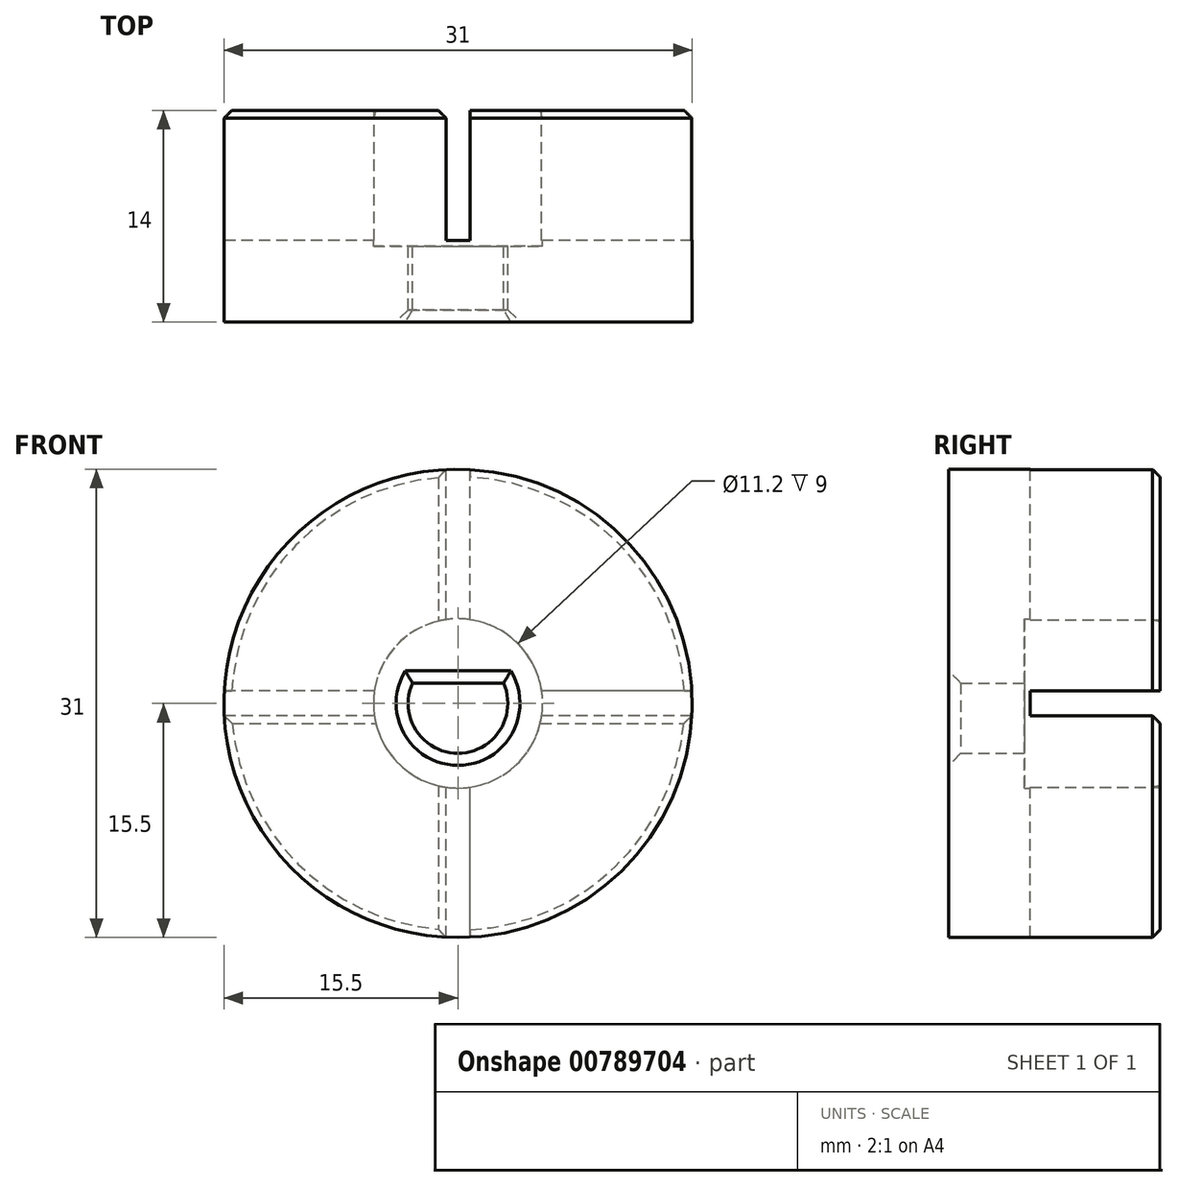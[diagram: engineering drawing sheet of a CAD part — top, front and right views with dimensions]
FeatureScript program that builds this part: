
annotation { "Feature Type Name" : "Feature", "Feature Type Description" : "" }
export const myFeature = defineFeature(function(context is Context, id is Id, definition is map)
    precondition{}
    {
        {
            var Q0;
            Q0=qCreatedBy(makeId("Front.planeOp"),FACE);
            var sketch = newSketch(context, id + "F0", { "sketchPlane" : qUnion([Q0])});
            skCircle(sketch, "E0", {"center": v(0, 0) * mm, "radius": 15.5 * mm});
            skArc(sketch, "E1", {"start": v(-3.01, 1.35) * mm, "mid": v(0, -3.3) * mm, "end": v(3.01, 1.35) * mm});
            skLineSegment(sketch, "E2", {"start": v(-3.01, 1.35) * mm, "end": v(3.01, 1.35) * mm});
            skSolve(sketch);
        }
        {
            var Q0;
            Q0=makeQuery(id+"F0.imprint","IMPRINT",FACE,{"disambiguationData":[TD([[makeQuery(id+"F0.imprint","IMPRINT",EDGE,{"derivedFrom":sQuery(id+"F0.wireOp",EDGE,"E0")}),1.0]])]});
            extrude(context, id + "F1", {"entities" : qUnion([Q0]), "depth" : 14 * mm, "offsetDistance" : 25 * mm});
        }
        {
            var Q0;
            Q0=qCreatedBy(makeId("Front.planeOp"),FACE);
            var sketch = newSketch(context, id + "F2", { "sketchPlane" : qUnion([Q0])});
            skLineSegment(sketch, "E3.bottom", {"start": v(18, -0.82) * mm, "end": v(-18, -0.83) * mm});
            skLineSegment(sketch, "E3.top", {"start": v(18, 0.83) * mm, "end": v(-18, 0.82) * mm});
            skLineSegment(sketch, "E3.left", {"start": v(18, -0.82) * mm, "end": v(18, 0.83) * mm});
            skLineSegment(sketch, "E3.right", {"start": v(-18, -0.83) * mm, "end": v(-18, 0.82) * mm});
            skSolve(sketch);
        }
        {
            var Q0;
            Q0=makeQuery(id+"F2.imprint","IMPRINT",FACE,{"disambiguationData":[TD([[makeQuery(id+"F2.imprint","IMPRINT",EDGE,{"derivedFrom":sQuery(id+"F2.wireOp",EDGE,"E3.bottom")}),-1.0]])]});
            extrude(context, id + "F3", {"entities" : qUnion([Q0]), "operationType" : NewBodyOperationType.REMOVE, "depth" : 8.6 * mm, "offsetDistance" : 25 * mm});
        }
        {
            var Q0;
            Q0=qCreatedBy(makeId("Front.planeOp"),FACE);
            var sketch = newSketch(context, id + "F4", { "sketchPlane" : qUnion([Q0])});
            skLineSegment(sketch, "E4.bottom", {"start": v(0.8, -20) * mm, "end": v(-0.8, -20) * mm});
            skLineSegment(sketch, "E4.top", {"start": v(0.8, 20) * mm, "end": v(-0.8, 20) * mm});
            skLineSegment(sketch, "E4.left", {"start": v(0.8, -20) * mm, "end": v(0.8, 20) * mm});
            skLineSegment(sketch, "E4.right", {"start": v(-0.8, -20) * mm, "end": v(-0.8, 20) * mm});
            skSolve(sketch);
        }
        {
            var Q0;
            Q0 = qSketchRegion(id + "F4", true);
            extrude(context, id + "F5", {"entities" : qUnion([Q0]), "operationType" : NewBodyOperationType.REMOVE, "depth" : 8.6 * mm, "offsetDistance" : 25 * mm});
        }
        {
            var Q0;
            Q0=qCreatedBy(makeId("Front.planeOp"),FACE);
            var sketch = newSketch(context, id + "F6", { "sketchPlane" : qUnion([Q0])});
            skCircle(sketch, "E5", {"center": v(0, 0) * mm, "radius": 5.6 * mm});
            skSolve(sketch);
        }
        {
            var Q0;
            Q0=makeQuery(id+"F6.imprint","IMPRINT",FACE,{"disambiguationData":[TD([[makeQuery(id+"F6.imprint","IMPRINT",EDGE,{"derivedFrom":sQuery(id+"F6.wireOp",EDGE,"E5")}),1.0]])]});
            extrude(context, id + "F7", {"entities" : qUnion([Q0]), "operationType" : NewBodyOperationType.REMOVE, "depth" : 9 * mm, "offsetDistance" : 25 * mm});
        }
        {
            var Q0;
            Q0=makeQuery(id+"F1.opExtrude","CAP_EDGE",EDGE,{"disambiguationData":[OSD([sQuery(id+"F0.wireOp",EDGE,"E2")])],"isStart":false});
            var Q1;
            Q1=makeQuery(id+"F1.opExtrude","CAP_EDGE",EDGE,{"disambiguationData":[OSD([sQuery(id+"F0.wireOp",EDGE,"E1")])],"isStart":false});
            chamfer(context, id + "F8", {"entities" : qUnion([Q0, Q1]), "width" : 0.8 * mm, "tangentPropagation" : true});
        }
        {
            var Q0;
            Q0=makeQuery(id+"F3.boolean.opBoolean","COPY",EDGE,{"disambiguationData":[OD(0.0)],"derivedFrom":makeQuery(id+"F3.opExtrude","CAP_EDGE",EDGE,{"disambiguationData":[OSD([sQuery(id+"F2.wireOp",EDGE,"E3.top")])],"isStart":true})});
            var Q1;
            Q1=makeQuery(id+"F3.boolean.opBoolean","COPY",EDGE,{"disambiguationData":[OD(0.0)],"derivedFrom":makeQuery(id+"F3.opExtrude","CAP_EDGE",EDGE,{"disambiguationData":[OSD([sQuery(id+"F2.wireOp",EDGE,"E3.bottom")])],"isStart":true})});
            var Q2;
            {var subQ1=sQuery(id+"F0.wireOp",EDGE,"E1");var subQ2=sQuery(id+"F4.wireOp",EDGE,"E4.right");Q2=makeQuery(id+"F5.boolean.opBoolean","COPY",EDGE,{"disambiguationData":[TD([makeQuery(id+"F1.opExtrude","SWEPT_FACE",FACE,{"disambiguationData":[OSD([subQ1])]})])],"derivedFrom":makeQuery(id+"F5.opExtrude","CAP_EDGE",EDGE,{"disambiguationData":[OSD([subQ2])],"isStart":true})});}
            var Q3;
            {var subQ1=sQuery(id+"F0.wireOp",EDGE,"E1");var subQ2=sQuery(id+"F4.wireOp",EDGE,"E4.left");Q3=makeQuery(id+"F5.boolean.opBoolean","COPY",EDGE,{"disambiguationData":[TD([makeQuery(id+"F1.opExtrude","SWEPT_FACE",FACE,{"disambiguationData":[OSD([subQ1])]})])],"derivedFrom":makeQuery(id+"F5.opExtrude","CAP_EDGE",EDGE,{"disambiguationData":[OSD([subQ2])],"isStart":true})});}
            var Q4;
            {var subQ3=sQuery(id+"F6.wireOp",EDGE,"E5");Q4=makeQuery(id+"F7.boolean.opBoolean","COPY",EDGE,{"disambiguationData":[TD([makeQuery(id+"F3.boolean.opBoolean","COPY",FACE,{"disambiguationData":[OD(1.0)],"derivedFrom":makeQuery(id+"F3.opExtrude","SWEPT_FACE",FACE,{"disambiguationData":[OSD([sQuery(id+"F2.wireOp",EDGE,"E3.bottom")])]})})])],"derivedFrom":makeQuery(id+"F7.opExtrude","CAP_EDGE",EDGE,{"disambiguationData":[OSD([subQ3])],"isStart":true})});}
            var Q5;
            Q5=makeQuery(id+"F3.boolean.opBoolean","COPY",EDGE,{"disambiguationData":[OD(1.0)],"derivedFrom":makeQuery(id+"F3.opExtrude","CAP_EDGE",EDGE,{"disambiguationData":[OSD([sQuery(id+"F2.wireOp",EDGE,"E3.bottom")])],"isStart":true})});
            var Q6;
            {var subQ0=sQuery(id+"F0.wireOp",EDGE,"E0");var subQ3=makeQuery(id+"F3.opExtrude","SWEPT_FACE",FACE,{"disambiguationData":[OSD([sQuery(id+"F2.wireOp",EDGE,"E3.bottom")])]});Q6=makeQuery(id+"F5.boolean.opBoolean","SPLIT",EDGE,{"disambiguationData":[TD([makeQuery(id+"F3.boolean.opBoolean","COPY",FACE,{"disambiguationData":[OD(1.0)],"derivedFrom":subQ3})])],"derivedFrom":makeQuery(id+"F3.boolean.opBoolean","SPLIT",EDGE,{"disambiguationData":[TD([subQ3])],"derivedFrom":makeQuery(id+"F1.opExtrude","CAP_EDGE",EDGE,{"disambiguationData":[OSD([subQ0])],"isStart":true})})});}
            var Q7;
            {var subQ0=sQuery(id+"F0.wireOp",EDGE,"E0");var subQ3=makeQuery(id+"F3.opExtrude","SWEPT_FACE",FACE,{"disambiguationData":[OSD([sQuery(id+"F2.wireOp",EDGE,"E3.bottom")])]});Q7=makeQuery(id+"F5.boolean.opBoolean","SPLIT",EDGE,{"disambiguationData":[TD([makeQuery(id+"F3.boolean.opBoolean","COPY",FACE,{"disambiguationData":[OD(0.0)],"derivedFrom":subQ3})])],"derivedFrom":makeQuery(id+"F3.boolean.opBoolean","SPLIT",EDGE,{"disambiguationData":[TD([subQ3])],"derivedFrom":makeQuery(id+"F1.opExtrude","CAP_EDGE",EDGE,{"disambiguationData":[OSD([subQ0])],"isStart":true})})});}
            var Q8;
            {var subQ3=sQuery(id+"F6.wireOp",EDGE,"E5");Q8=makeQuery(id+"F7.boolean.opBoolean","COPY",EDGE,{"disambiguationData":[TD([makeQuery(id+"F3.boolean.opBoolean","COPY",FACE,{"disambiguationData":[OD(0.0)],"derivedFrom":makeQuery(id+"F3.opExtrude","SWEPT_FACE",FACE,{"disambiguationData":[OSD([sQuery(id+"F2.wireOp",EDGE,"E3.bottom")])]})})])],"derivedFrom":makeQuery(id+"F7.opExtrude","CAP_EDGE",EDGE,{"disambiguationData":[OSD([subQ3])],"isStart":true})});}
            var Q9;
            {var subQ3=sQuery(id+"F6.wireOp",EDGE,"E5");Q9=makeQuery(id+"F7.boolean.opBoolean","COPY",EDGE,{"disambiguationData":[TD([makeQuery(id+"F3.boolean.opBoolean","COPY",FACE,{"disambiguationData":[OD(0.0)],"derivedFrom":makeQuery(id+"F3.opExtrude","SWEPT_FACE",FACE,{"disambiguationData":[OSD([sQuery(id+"F2.wireOp",EDGE,"E3.top")])]})})])],"derivedFrom":makeQuery(id+"F7.opExtrude","CAP_EDGE",EDGE,{"disambiguationData":[OSD([subQ3])],"isStart":true})});}
            var Q10;
            {var subQ0=sQuery(id+"F0.wireOp",EDGE,"E0");var subQ3=makeQuery(id+"F3.opExtrude","SWEPT_FACE",FACE,{"disambiguationData":[OSD([sQuery(id+"F2.wireOp",EDGE,"E3.top")])]});Q10=makeQuery(id+"F5.boolean.opBoolean","SPLIT",EDGE,{"disambiguationData":[TD([makeQuery(id+"F3.boolean.opBoolean","COPY",FACE,{"disambiguationData":[OD(0.0)],"derivedFrom":subQ3})])],"derivedFrom":makeQuery(id+"F3.boolean.opBoolean","SPLIT",EDGE,{"disambiguationData":[TD([subQ3])],"derivedFrom":makeQuery(id+"F1.opExtrude","CAP_EDGE",EDGE,{"disambiguationData":[OSD([subQ0])],"isStart":true})})});}
            var Q11;
            {var subQ1=sQuery(id+"F0.wireOp",EDGE,"E2");var subQ2=sQuery(id+"F4.wireOp",EDGE,"E4.right");Q11=makeQuery(id+"F5.boolean.opBoolean","COPY",EDGE,{"disambiguationData":[TD([makeQuery(id+"F1.opExtrude","SWEPT_FACE",FACE,{"disambiguationData":[OSD([subQ1])]})])],"derivedFrom":makeQuery(id+"F5.opExtrude","CAP_EDGE",EDGE,{"disambiguationData":[OSD([subQ2])],"isStart":true})});}
            var Q12;
            {var subQ1=sQuery(id+"F0.wireOp",EDGE,"E2");var subQ2=sQuery(id+"F4.wireOp",EDGE,"E4.left");Q12=makeQuery(id+"F5.boolean.opBoolean","COPY",EDGE,{"disambiguationData":[TD([makeQuery(id+"F1.opExtrude","SWEPT_FACE",FACE,{"disambiguationData":[OSD([subQ1])]})])],"derivedFrom":makeQuery(id+"F5.opExtrude","CAP_EDGE",EDGE,{"disambiguationData":[OSD([subQ2])],"isStart":true})});}
            var Q13;
            {var subQ3=sQuery(id+"F6.wireOp",EDGE,"E5");Q13=makeQuery(id+"F7.boolean.opBoolean","COPY",EDGE,{"disambiguationData":[TD([makeQuery(id+"F3.boolean.opBoolean","COPY",FACE,{"disambiguationData":[OD(1.0)],"derivedFrom":makeQuery(id+"F3.opExtrude","SWEPT_FACE",FACE,{"disambiguationData":[OSD([sQuery(id+"F2.wireOp",EDGE,"E3.top")])]})})])],"derivedFrom":makeQuery(id+"F7.opExtrude","CAP_EDGE",EDGE,{"disambiguationData":[OSD([subQ3])],"isStart":true})});}
            var Q14;
            Q14=makeQuery(id+"F3.boolean.opBoolean","COPY",EDGE,{"disambiguationData":[OD(1.0)],"derivedFrom":makeQuery(id+"F3.opExtrude","CAP_EDGE",EDGE,{"disambiguationData":[OSD([sQuery(id+"F2.wireOp",EDGE,"E3.top")])],"isStart":true})});
            var Q15;
            {var subQ0=sQuery(id+"F0.wireOp",EDGE,"E0");var subQ3=makeQuery(id+"F3.opExtrude","SWEPT_FACE",FACE,{"disambiguationData":[OSD([sQuery(id+"F2.wireOp",EDGE,"E3.top")])]});Q15=makeQuery(id+"F5.boolean.opBoolean","SPLIT",EDGE,{"disambiguationData":[TD([makeQuery(id+"F3.boolean.opBoolean","COPY",FACE,{"disambiguationData":[OD(1.0)],"derivedFrom":subQ3})])],"derivedFrom":makeQuery(id+"F3.boolean.opBoolean","SPLIT",EDGE,{"disambiguationData":[TD([subQ3])],"derivedFrom":makeQuery(id+"F1.opExtrude","CAP_EDGE",EDGE,{"disambiguationData":[OSD([subQ0])],"isStart":true})})});}
            chamfer(context, id + "F9", {"entities" : qUnion([Q0, Q1, Q2, Q3, Q4, Q5, Q6, Q7, Q8, Q9, Q10, Q11, Q12, Q13, Q14, Q15]), "width" : 0.5 * mm, "tangentPropagation" : true});
        }
    });
